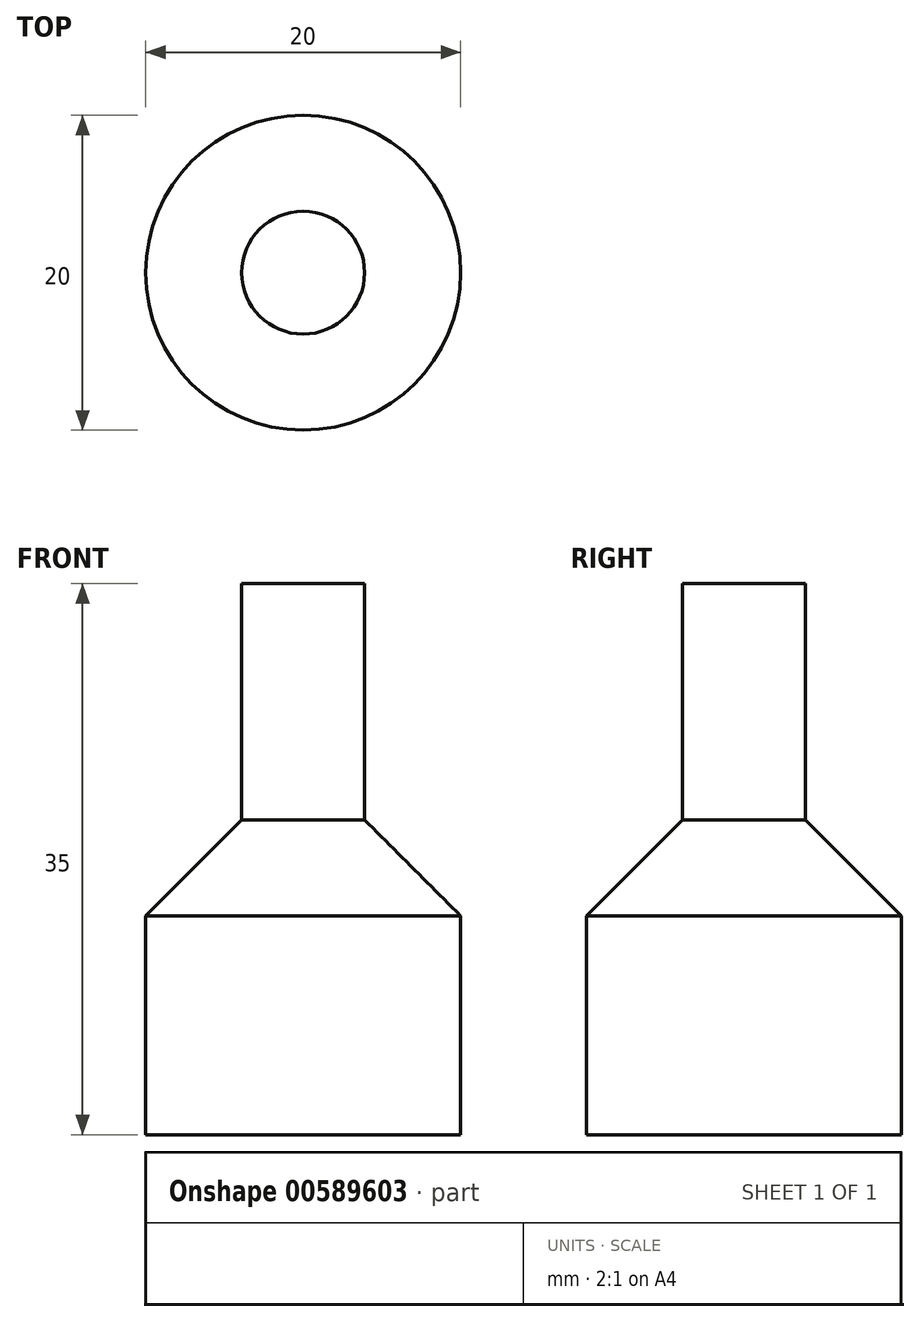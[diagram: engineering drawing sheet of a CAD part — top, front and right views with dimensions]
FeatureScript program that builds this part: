
annotation { "Feature Type Name" : "Feature", "Feature Type Description" : "" }
export const myFeature = defineFeature(function(context is Context, id is Id, definition is map)
    precondition{}
    {
        {
            var Q0;
            Q0=qCreatedBy(makeId("Top.planeOp"),FACE);
            var sketch = newSketch(context, id + "F0", { "sketchPlane" : qUnion([Q0])});
            skCircle(sketch, "E0", {"center": v(0, 0) * mm, "radius": 3.9 * mm});
            skSolve(sketch);
        }
        {
            var Q0;
            Q0 = qSketchRegion(id + "F0", true);
            extrude(context, id + "F1", {"entities" : qUnion([Q0]), "depth" : 15 * mm, "offsetDistance" : 25 * mm});
        }
        {
            var Q0;
            Q0=qCreatedBy(makeId("Top.planeOp"),FACE);
            var sketch = newSketch(context, id + "F2", { "sketchPlane" : qUnion([Q0])});
            skCircle(sketch, "E1", {"center": v(0, 0) * mm, "radius": 10 * mm});
            skSolve(sketch);
        }
        {
            var Q0;
            Q0 = qSketchRegion(id + "F2", true);
            extrude(context, id + "F3", {"entities" : qUnion([Q0]), "operationType" : NewBodyOperationType.ADD, "oppositeDirection" : true, "depth" : 20 * mm, "offsetDistance" : 25 * mm});
        }
        {
            var Q0;
            Q0=makeQuery(id+"F3.opExtrude","CAP_EDGE",EDGE,{"disambiguationData":[OSD([sQuery(id+"F2.wireOp",EDGE,"E1")])],"isStart":true});
            chamfer(context, id + "F4", {"entities" : qUnion([Q0]), "width" : 6.1 * mm, "tangentPropagation" : true});
        }
    });
